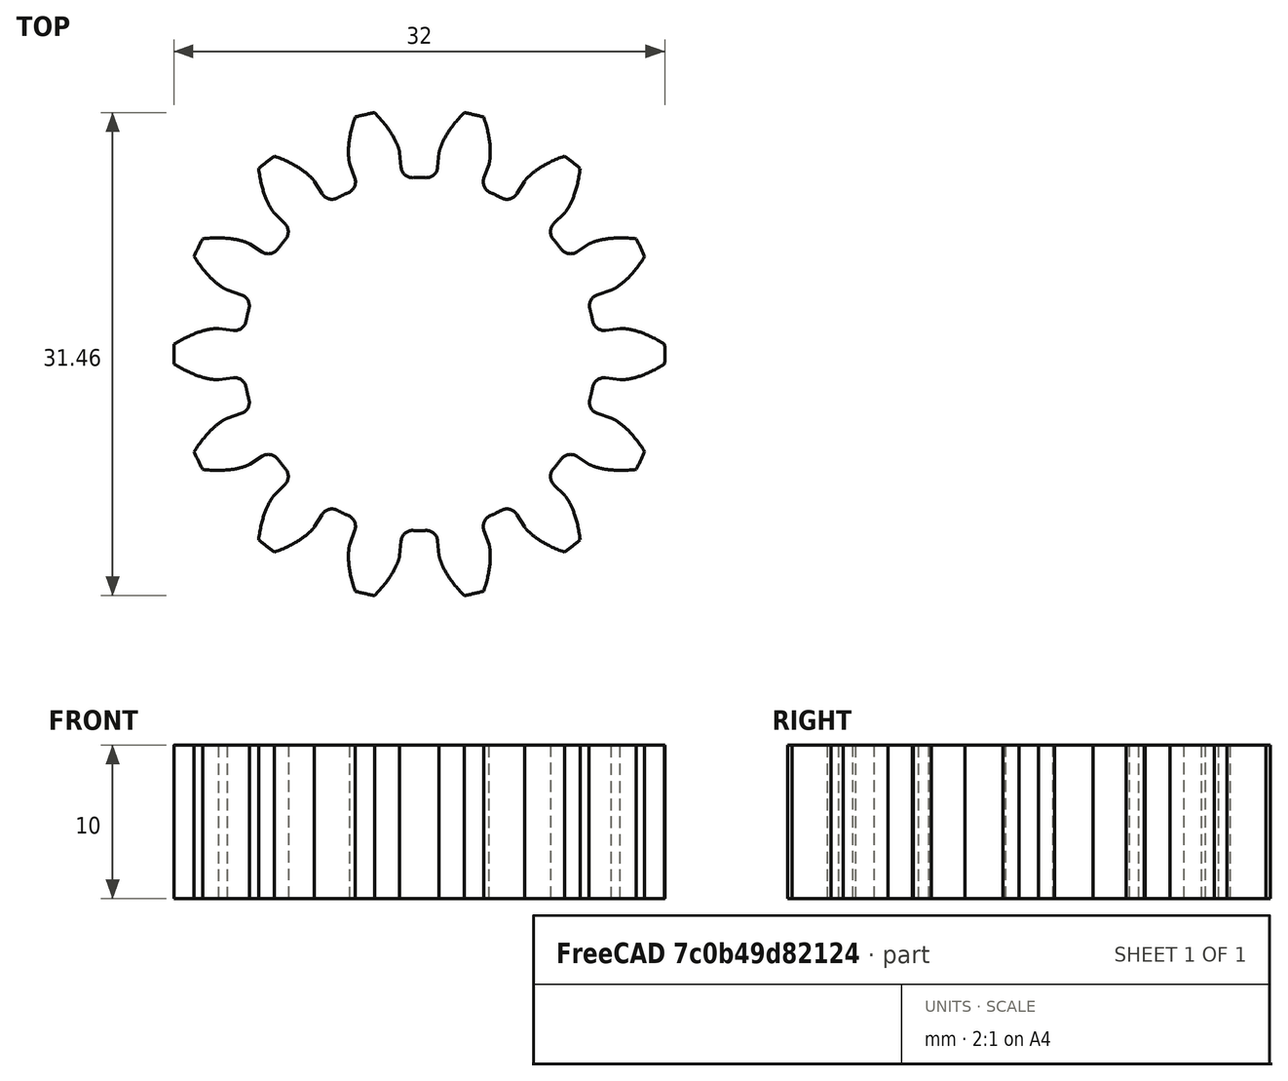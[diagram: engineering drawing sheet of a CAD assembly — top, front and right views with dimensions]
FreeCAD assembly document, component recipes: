
FREECAD ASSEMBLY — COMPONENT RECIPES ("assambly_gears_2")

This assembly document has 3 components, labeled P0..P2 below (a component is one placed body or linked part). 2 of them carry a construction recipe — the FreeCAD feature program that regenerates the part from scratch, quoted from this document or its linked companion documents; the rest are supplied as boundary geometry only. No exploded tour is included for this assembly.
COMPONENT P0 — geometry summary ("Assembly"; no construction recipe available for this part):
  bounding box: 134.0 x 134.0 x 10.0 mm
  tessellated surface: 11,040 triangles
  volume: 399643493761140770789286686410663538032367540430844958718825833876287312795002033530069303978941743104 mm^3 (222608370336316376326182104883907955530147253316911590893777551514307979275558573097014829351174144% of its bounding box)
  symmetry: 2-fold rotationally symmetric about the x axis; 2-fold rotationally symmetric about the y axis; 2-fold rotationally symmetric about the z axis; mirror-symmetric across its x mid-plane, y mid-plane, z mid-plane
COMPONENT P1 — recipe-attached ("Body_14t_pd", modeled in this document).
Construction recipe (the document's own serialized feature program — sketch geometry with constraints, then the solid features built on it; lengths are millimeters unless a unit is written):

FEATURE [PartDesign::FeatureBase] BaseFeature
FEATURE [PartDesign::CoordinateSystem] LCS_g_14t
  AttacherType = Attacher::AttachEngine3D
  MapMode = 45
  Placement = pos=(1.2e-15,-4.5e-15,10) rot=(0,0,1;0rad)
  Support = -> [BaseFeature]
FEATURE [PartDesign::Body] Body  label="Body_14t_pd"
  Group = -> [BaseFeature,LCS_g_14t]
  Origin = -> Origin001
  Tip = -> BaseFeature
COMPONENT P2 — recipe-attached ("Body_in_gear", modeled in this document).
Construction recipe (the document's own serialized feature program — sketch geometry with constraints, then the solid features built on it; lengths are millimeters unless a unit is written):

FEATURE [Part::Part2DObjectPython] InvoluteGear  # Draft 2D object (typed FeaturePython)
  ExternalGear = true
  HighPrecision = true
  Modules = 2
  NumberOfTeeth = 60
  PressureAngle = 20
FEATURE [PartDesign::FeatureBase] BaseFeature001
  BaseFeature = -> Cut
FEATURE [PartDesign::CoordinateSystem] LCS_in_g
  AttacherType = Attacher::AttachEngine3D
  MapMode = 5
  Support = -> [Cut]
FEATURE [PartDesign::Body] Body001  label="Body_in_gear"
  BaseFeature = -> Cut
  Group = -> [BaseFeature001,InvoluteGear,LCS_in_g]
  Origin = -> Origin002
  Tip = -> BaseFeature001
PROVENANCE & LICENSES
A FreeCAD (.FCStd) document from a public repository crawl; recipes are the document's own serialized feature recipes (and, for linked parts, companion documents' recipes).
License: as declared in the source repository (recorded in the dataset sidecar).
